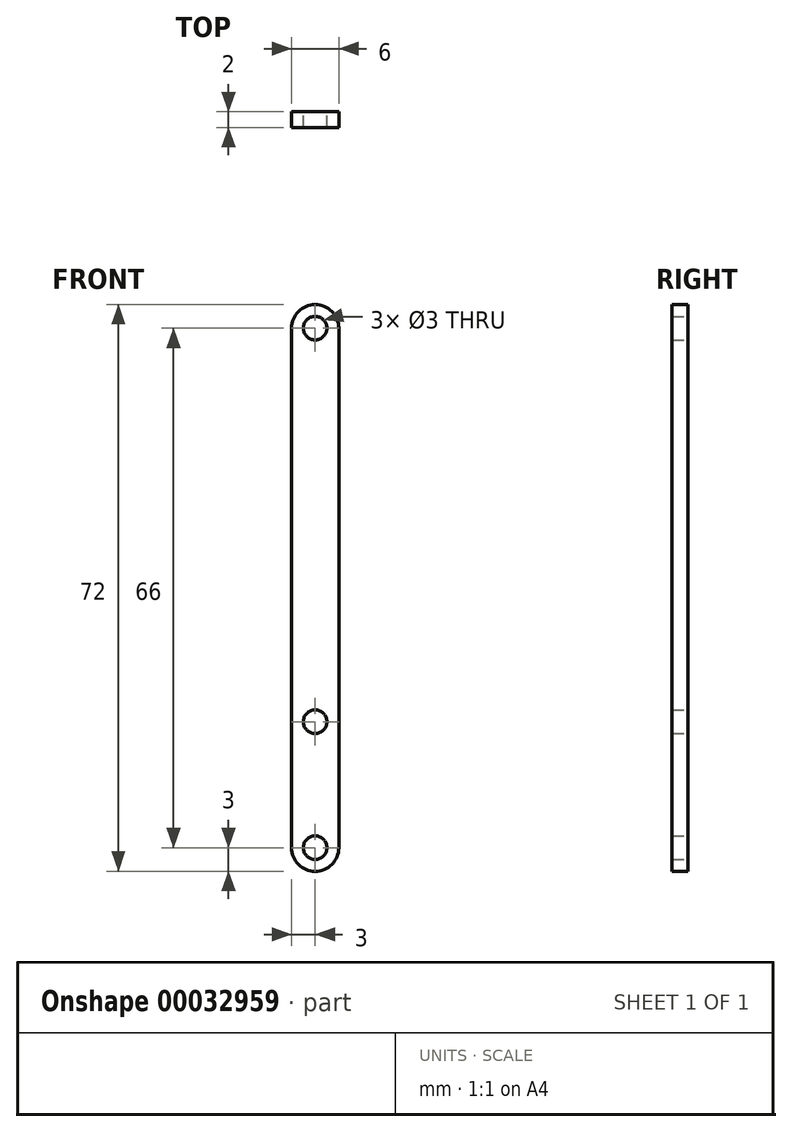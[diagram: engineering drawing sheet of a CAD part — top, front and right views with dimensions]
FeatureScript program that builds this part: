
annotation { "Feature Type Name" : "Feature", "Feature Type Description" : "" }
export const myFeature = defineFeature(function(context is Context, id is Id, definition is map)
    precondition{}
    {
        {
            var Q0;
            Q0=qCreatedBy(makeId("Front.planeOp"),FACE);
            var sketch = newSketch(context, id + "F0", { "sketchPlane" : qUnion([Q0])});
            skLineSegment(sketch, "E0.rect.left", {"start": v(3, -25) * mm, "end": v(3, 25) * mm});
            skLineSegment(sketch, "E0.rect.right", {"start": v(-3, -25) * mm, "end": v(-3, 25) * mm});
            skPoint(sketch, "E0.rect.middle", {"position": v(0, 0) * mm});
            skArc(sketch, "E1", {"start": v(3, 25) * mm, "mid": v(0, 28) * mm, "end": v(-3, 25) * mm});
            skCircle(sketch, "E2", {"center": v(0, 25) * mm, "radius": 1.5 * mm});
            skCircle(sketch, "E3.MirrorC", {"center": v(0, -25) * mm, "radius": 1.5 * mm});
            skCircle(sketch, "E4", {"center": v(0, -41) * mm, "radius": 1.5 * mm});
            skArc(sketch, "E5", {"start": v(-3, -41) * mm, "mid": v(0, -44) * mm, "end": v(3, -41) * mm});
            skLineSegment(sketch, "E6", {"start": v(-3, -25) * mm, "end": v(-3, -41) * mm});
            skLineSegment(sketch, "E7", {"start": v(3, -25) * mm, "end": v(3, -41) * mm});
            skPoint(sketch, "E8.MirrorCS.end.orphan", {"position": v(-3, -25) * mm});
            skPoint(sketch, "E8.MirrorCS.start.orphan", {"position": v(3, -25) * mm});
            skSolve(sketch);
        }
        {
            var Q0;
            Q0=qSketchRegion(id+"F0",true);
            extrude(context, id + "F1", {"entities" : qUnion([Q0]), "depth" : 2 * mm});
        }
    });
